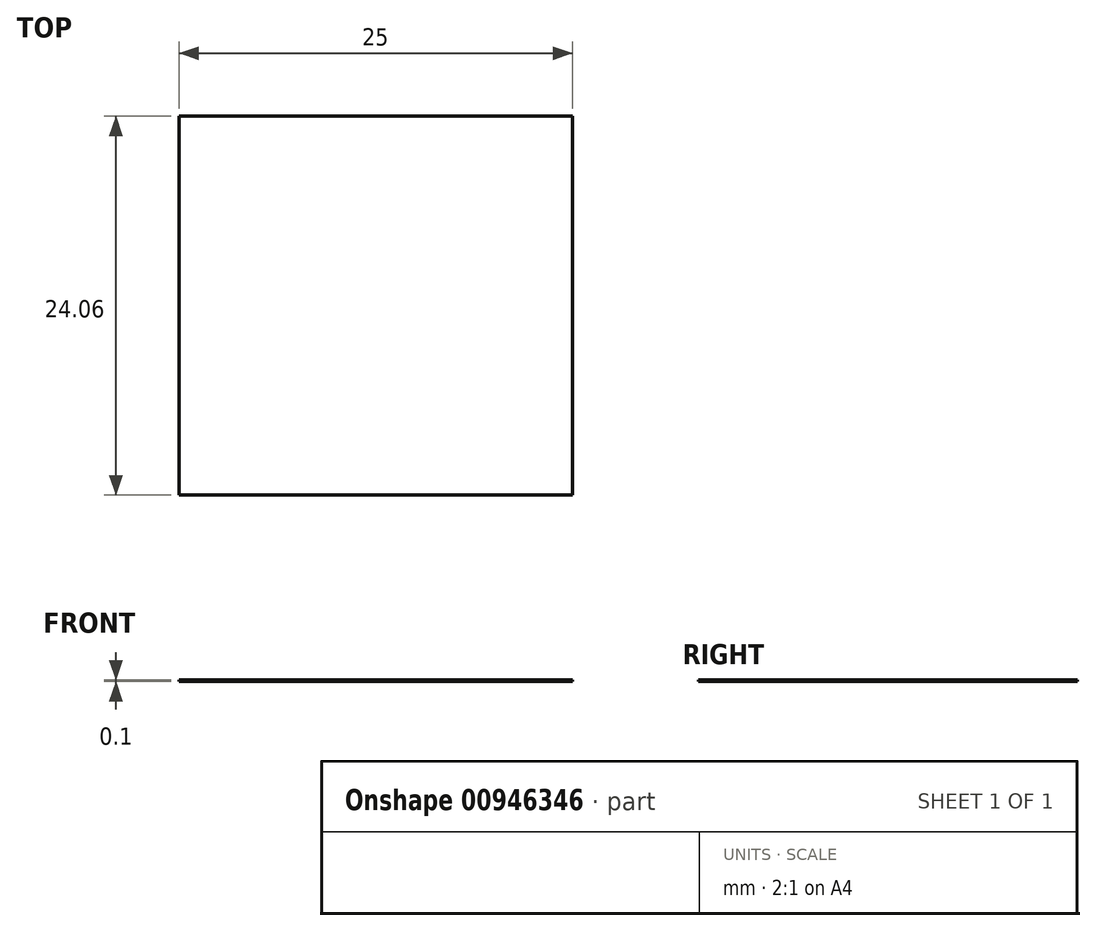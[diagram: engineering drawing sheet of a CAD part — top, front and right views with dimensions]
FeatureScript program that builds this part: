
annotation { "Feature Type Name" : "Feature", "Feature Type Description" : "" }
export const myFeature = defineFeature(function(context is Context, id is Id, definition is map)
    precondition{}
    {
        {
            var Q0;
            Q0=qCreatedBy(makeId("Top.planeOp"),FACE);
            var sketch = newSketch(context, id + "F0", { "sketchPlane" : qUnion([Q0])});
            skLineSegment(sketch, "E0.bottom", {"start": v(12.5, -12.03) * mm, "end": v(-12.5, -12.03) * mm});
            skLineSegment(sketch, "E0.top", {"start": v(12.5, 12.03) * mm, "end": v(-12.5, 12.03) * mm});
            skLineSegment(sketch, "E0.left", {"start": v(12.5, -12.03) * mm, "end": v(12.5, 12.03) * mm});
            skLineSegment(sketch, "E0.right", {"start": v(-12.5, -12.03) * mm, "end": v(-12.5, 12.03) * mm});
            skPoint(sketch, "E0.middle", {"position": v(0, 0) * mm});
            skSolve(sketch);
        }
        {
            var Q0;
            Q0=makeQuery(id+"F0.imprint","IMPRINT",FACE,{"disambiguationData":[TD([[makeQuery(id+"F0.imprint","IMPRINT",EDGE,{"derivedFrom":sQuery(id+"F0.wireOp",EDGE,"E0.bottom")}),-1.0]])]});
            extrude(context, id + "F1", {"entities" : qUnion([Q0]), "depth" : 0.1 * mm, "offsetDistance" : 25 * mm});
        }
    });
